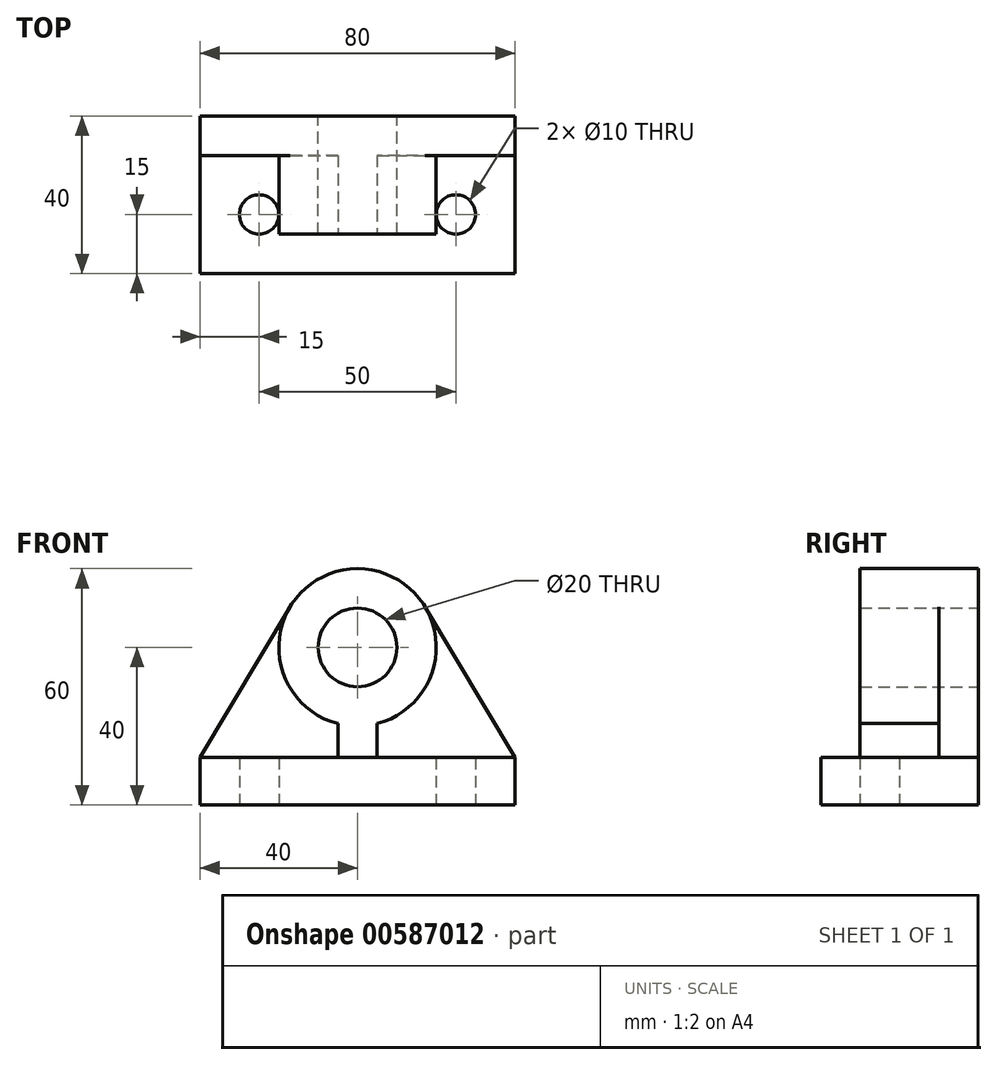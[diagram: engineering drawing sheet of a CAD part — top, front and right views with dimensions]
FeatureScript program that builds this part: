
annotation { "Feature Type Name" : "Feature", "Feature Type Description" : "" }
export const myFeature = defineFeature(function(context is Context, id is Id, definition is map)
    precondition{}
    {
        {
            var Q0;
            Q0=qCreatedBy(makeId("Top.planeOp"),FACE);
            var sketch = newSketch(context, id + "F0", { "sketchPlane" : qUnion([Q0])});
            skLineSegment(sketch, "E0.bottom", {"start": v(40, 20) * mm, "end": v(-40, 20) * mm});
            skLineSegment(sketch, "E0.top", {"start": v(40, -20) * mm, "end": v(-40, -20) * mm});
            skLineSegment(sketch, "E0.left", {"start": v(40, 20) * mm, "end": v(40, -20) * mm});
            skLineSegment(sketch, "E0.right", {"start": v(-40, 20) * mm, "end": v(-40, -20) * mm});
            skPoint(sketch, "E0.middle", {"position": v(0, 0) * mm});
            skCircle(sketch, "E1", {"center": v(-25, -5) * mm, "radius": 5 * mm});
            skCircle(sketch, "E2.MirrorC", {"center": v(25, -5) * mm, "radius": 5 * mm});
            skSolve(sketch);
        }
        {
            var Q0;
            Q0 = qSketchRegion(id + "F0", true);
            extrude(context, id + "F1", {"entities" : qUnion([Q0]), "depth" : 12 * mm, "offsetDistance" : 25 * mm});
        }
        {
            var Q0;
            Q0=makeQuery(id+"F1.opExtrude","SWEPT_FACE",FACE,{"disambiguationData":[OSD([sQuery(id+"F0.wireOp",EDGE,"E0.bottom")])]});
            var sketch = newSketch(context, id + "F2", { "sketchPlane" : qUnion([Q0])});
            skLineSegment(sketch, "E3.0.0", {"start": v(-40, 0) * mm, "end": v(40, 0) * mm});
            skLineSegment(sketch, "E3.0.1", {"start": v(40, 0) * mm, "end": v(40, 12) * mm});
            skLineSegment(sketch, "E3.0.2", {"start": v(40, 12) * mm, "end": v(-40, 12) * mm});
            skLineSegment(sketch, "E3.0.3", {"start": v(-40, 12) * mm, "end": v(-40, 0) * mm});
            skCircle(sketch, "E4", {"center": v(0, 40) * mm, "radius": 10 * mm});
            skCircle(sketch, "E5", {"center": v(0, 40) * mm, "radius": 20 * mm});
            skSolve(sketch);
        }
        {
            var Q0;
            Q0=makeQuery(id+"F2.imprint","IMPRINT",FACE,{"disambiguationData":[TD([[makeQuery(id+"F2.imprint","IMPRINT",EDGE,{"derivedFrom":sQuery(id+"F2.wireOp",EDGE,"E4")}),-1.0]])]});
            extrude(context, id + "F3", {"entities" : qUnion([Q0]), "oppositeDirection" : true, "depth" : 30 * mm, "offsetDistance" : 25 * mm});
        }
        {
            var Q0;
            Q0=makeQuery(id+"F3.opExtrude","CAP_FACE",FACE,{"disambiguationData":[OSD([sQuery(id+"F2.wireOp",EDGE,"E4"),sQuery(id+"F2.wireOp",EDGE,"E5")])],"isStart":true});
            var sketch = newSketch(context, id + "F4", { "sketchPlane" : qUnion([Q0])});
            skLineSegment(sketch, "E6.0.0", {"start": v(-40, 0) * mm, "end": v(40, 0) * mm});
            skLineSegment(sketch, "E6.0.1", {"start": v(40, 0) * mm, "end": v(40, 12) * mm});
            skLineSegment(sketch, "E6.0.2", {"start": v(40, 12) * mm, "end": v(-40, 12) * mm});
            skLineSegment(sketch, "E6.0.3", {"start": v(-40, 12) * mm, "end": v(-40, 0) * mm});
            skLineSegment(sketch, "E7", {"start": v(-40, 12) * mm, "end": v(-6.26, 68.54) * mm});
            skLineSegment(sketch, "E8", {"start": v(40, 12) * mm, "end": v(9.78, 62.64) * mm});
            skSolve(sketch);
        }
        {
            var Q0;
            {var subQ0=sQuery(id+"F4.wireOp",EDGE,"E6.0.2");Q0=makeQuery(id+"F4.imprint","IMPRINT",FACE,{"disambiguationData":[TD([[makeQuery(id+"F4.imprint","IMPRINT",EDGE,{"derivedFrom":subQ0}),-1.0]])]});}
            extrude(context, id + "F5", {"entities" : qUnion([Q0]), "oppositeDirection" : true, "depth" : 10 * mm, "offsetDistance" : 25 * mm});
        }
        {
            var Q0;
            Q0=makeQuery(id+"F3.opExtrude","CAP_FACE",FACE,{"disambiguationData":[OSD([sQuery(id+"F2.wireOp",EDGE,"E4"),sQuery(id+"F2.wireOp",EDGE,"E5")])],"isStart":false});
            var sketch = newSketch(context, id + "F6", { "sketchPlane" : qUnion([Q0])});
            skLineSegment(sketch, "E9.0.0", {"start": v(-40, 0) * mm, "end": v(40, 0) * mm});
            skLineSegment(sketch, "E9.0.1", {"start": v(40, 0) * mm, "end": v(40, 12) * mm});
            skLineSegment(sketch, "E9.0.2", {"start": v(40, 12) * mm, "end": v(-40, 12) * mm});
            skLineSegment(sketch, "E9.0.3", {"start": v(-40, 12) * mm, "end": v(-40, 0) * mm});
            skLineSegment(sketch, "E10", {"start": v(0, 20) * mm, "end": v(0, 12) * mm});
            skLineSegment(sketch, "E11", {"start": v(5, 20.64) * mm, "end": v(5, 12) * mm});
            skLineSegment(sketch, "E12.MirrorCS", {"start": v(-5, 20.64) * mm, "end": v(-5, 12) * mm});
            skSolve(sketch);
        }
        {
            var Q0;
            {var subQ0=sQuery(id+"F6.wireOp",EDGE,"E10");Q0=makeQuery(id+"F6.imprint","IMPRINT",FACE,{"disambiguationData":[TD([[makeQuery(id+"F6.imprint","IMPRINT",EDGE,{"derivedFrom":subQ0}),1.0]])]});}
            var Q1;
            {var subQ0=sQuery(id+"F6.wireOp",EDGE,"E10");Q1=makeQuery(id+"F6.imprint","IMPRINT",FACE,{"disambiguationData":[TD([[makeQuery(id+"F6.imprint","IMPRINT",EDGE,{"derivedFrom":subQ0}),-1.0]])]});}
            extrude(context, id + "F7", {"entities" : qUnion([Q0, Q1]), "operationType" : NewBodyOperationType.ADD, "oppositeDirection" : true, "depth" : 25 * mm, "offsetDistance" : 25 * mm});
        }
    });
